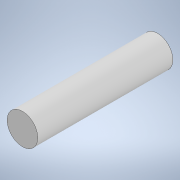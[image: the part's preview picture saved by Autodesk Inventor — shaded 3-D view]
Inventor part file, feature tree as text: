
AUTODESK INVENTOR PART (.ipt)
format: ipt  version: 2021 (Build 250183000, 183)  size: 89,600 bytes
history: native  units: mm
features: extrude x1, sketch x1
ambient origin geometry x8: Origin, YZ Plane, XZ Plane, XY Plane, X Axis, Y Axis, Z Axis, Center Point
bodies: Solid1 (feature_tree)
feature tree (2):
  extrude  "Extrusion1"  Depth=220.0mm TaperAngle=0.0deg
  sketch  "Sketch1"  dims[d0=50.0mm d1=220.0mm d2=0.0mm]
